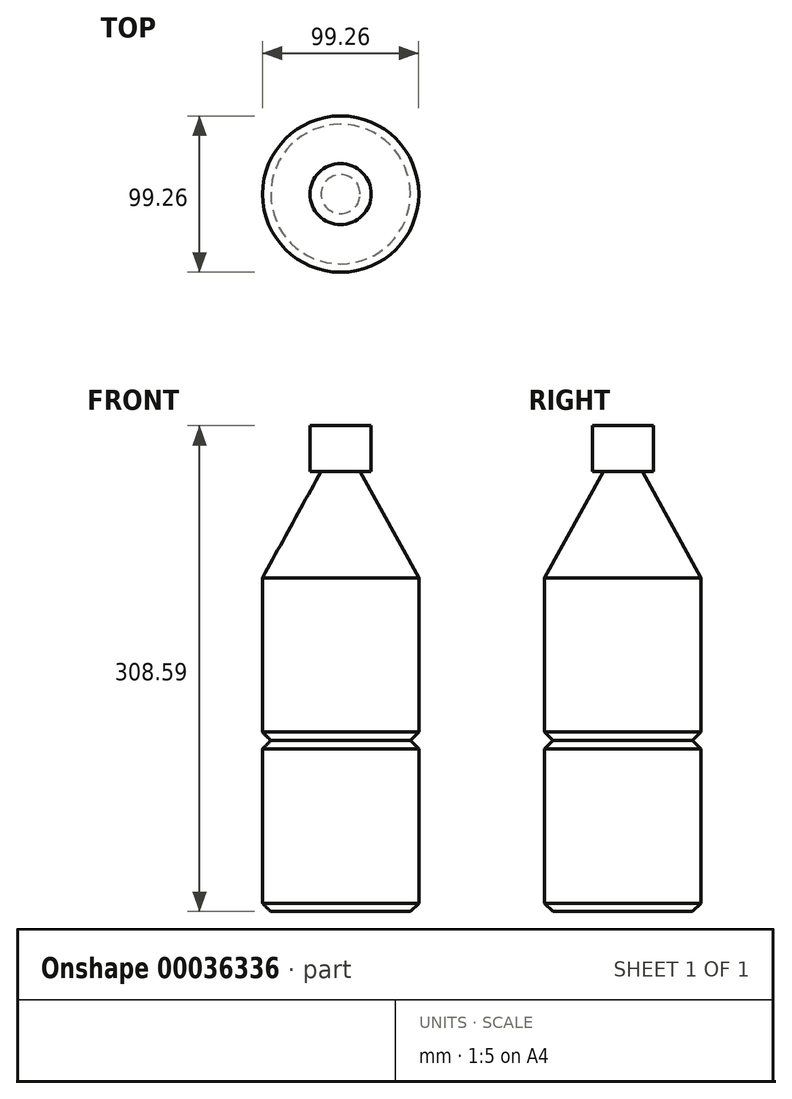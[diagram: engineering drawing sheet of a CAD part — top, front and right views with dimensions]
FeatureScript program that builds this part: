
annotation { "Feature Type Name" : "Feature", "Feature Type Description" : "" }
export const myFeature = defineFeature(function(context is Context, id is Id, definition is map)
    precondition{}
    {
        {
            var Q0;
            Q0=qCreatedBy(makeId("Front.planeOp"),FACE);
            var sketch = newSketch(context, id + "F0", { "sketchPlane" : qUnion([Q0])});
            skLineSegment(sketch, "E0", {"start": v(-49.63, 42.75) * mm, "end": v(-49.63, -55.27) * mm});
            skLineSegment(sketch, "E1", {"start": v(-49.63, -55.27) * mm, "end": v(-44.31, -60.6) * mm});
            skLineSegment(sketch, "E2.MirrorCS", {"start": v(-49.63, -163.93) * mm, "end": v(-49.63, -65.92) * mm});
            skLineSegment(sketch, "E3.MirrorCS", {"start": v(-49.63, -65.92) * mm, "end": v(-44.31, -60.6) * mm});
            skLineSegment(sketch, "E4", {"start": v(-49.63, -163.93) * mm, "end": v(-49.63, -114.93) * mm});
            skLineSegment(sketch, "E5.MirrorCS", {"start": v(-49.63, -163.93) * mm, "end": v(-44.31, -169.26) * mm});
            skLineSegment(sketch, "E6", {"start": v(-44.31, -169.26) * mm, "end": v(0, -169.26) * mm});
            skLineSegment(sketch, "E7", {"start": v(0, -169.26) * mm, "end": v(-22.16, -169.26) * mm});
            skLineSegment(sketch, "E8", {"start": v(-22.16, -169.26) * mm, "end": v(0, -169.26) * mm});
            skLineSegment(sketch, "E9", {"start": v(0, -169.26) * mm, "end": v(0, -110.23) * mm});
            skLineSegment(sketch, "E10.MirrorCS", {"start": v(22.16, -169.26) * mm, "end": v(0, -169.26) * mm});
            skLineSegment(sketch, "E11.MirrorCS", {"start": v(44.31, -169.26) * mm, "end": v(0, -169.26) * mm});
            skLineSegment(sketch, "E12.MirrorCS", {"start": v(49.63, -163.93) * mm, "end": v(44.31, -169.26) * mm});
            skLineSegment(sketch, "E13.MirrorCS", {"start": v(49.63, -163.93) * mm, "end": v(49.63, -114.93) * mm});
            skLineSegment(sketch, "E14.MirrorCS", {"start": v(49.63, -163.93) * mm, "end": v(49.63, -65.92) * mm});
            skLineSegment(sketch, "E15.MirrorCS", {"start": v(49.63, -65.92) * mm, "end": v(44.31, -60.6) * mm});
            skLineSegment(sketch, "E16.MirrorCS", {"start": v(49.63, -55.27) * mm, "end": v(44.31, -60.6) * mm});
            skLineSegment(sketch, "E17.MirrorCS", {"start": v(49.63, 42.75) * mm, "end": v(49.63, -55.27) * mm});
            skLineSegment(sketch, "E18", {"start": v(0, -110.23) * mm, "end": v(0, 42.75) * mm});
            skLineSegment(sketch, "E19", {"start": v(49.63, 42.75) * mm, "end": v(-49.63, 42.75) * mm});
            skLineSegment(sketch, "E20", {"start": v(-12.4, 110.27) * mm, "end": v(12.4, 110.27) * mm});
            skLineSegment(sketch, "E21", {"start": v(12.4, 110.27) * mm, "end": v(49.63, 42.75) * mm});
            skLineSegment(sketch, "E22", {"start": v(-12.4, 110.27) * mm, "end": v(-49.63, 42.75) * mm});
            skLineSegment(sketch, "E23", {"start": v(-12.4, 110.27) * mm, "end": v(-19.42, 110.27) * mm});
            skLineSegment(sketch, "E24", {"start": v(-19.42, 110.27) * mm, "end": v(-19.42, 139.33) * mm});
            skLineSegment(sketch, "E25", {"start": v(-19.42, 139.33) * mm, "end": v(0, 139.33) * mm});
            skLineSegment(sketch, "E26", {"start": v(0, 139.33) * mm, "end": v(0, 110.27) * mm});
            skLineSegment(sketch, "E27.MirrorCS", {"start": v(19.42, 110.27) * mm, "end": v(19.42, 139.33) * mm});
            skLineSegment(sketch, "E28.MirrorCS", {"start": v(19.42, 139.33) * mm, "end": v(0, 139.33) * mm});
            skLineSegment(sketch, "E29.MirrorCS", {"start": v(12.4, 110.27) * mm, "end": v(19.42, 110.27) * mm});
            skLineSegment(sketch, "E30", {"start": v(0, 42.75) * mm, "end": v(0, 110.27) * mm});
            skSolve(sketch);
        }
        {
            var Q0;
            {var subQ7=sQuery(id+"F0.wireOp",EDGE,"E9");Q0=makeQuery(id+"F0.imprint","IMPRINT",FACE,{"disambiguationData":[TD([[makeQuery(id+"F0.imprint","IMPRINT",EDGE,{"derivedFrom":subQ7}),-1.0]])]});}
            var Q1;
            {var subQ1=sQuery(id+"F0.wireOp",EDGE,"E21");Q1=makeQuery(id+"F0.imprint","IMPRINT",FACE,{"disambiguationData":[TD([[makeQuery(id+"F0.imprint","IMPRINT",EDGE,{"derivedFrom":subQ1}),-1.0]])]});}
            var Q2;
            {var subQ1=sQuery(id+"F0.wireOp",EDGE,"E26");Q2=makeQuery(id+"F0.imprint","IMPRINT",FACE,{"disambiguationData":[TD([[makeQuery(id+"F0.imprint","IMPRINT",EDGE,{"derivedFrom":subQ1}),1.0]])]});}
            var Q3;
            Q3=sQuery(id+"F0.wireOp",EDGE,"E9");
            revolve(context, id + "F1", {"entities" : qUnion([Q0, Q1, Q2]), "axis" : qUnion([Q3]), "revolveType" : RevolveType.FULL});
        }
    });
